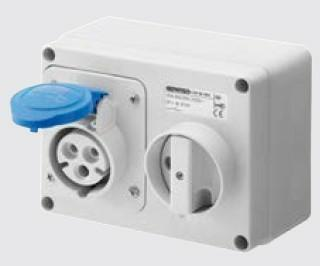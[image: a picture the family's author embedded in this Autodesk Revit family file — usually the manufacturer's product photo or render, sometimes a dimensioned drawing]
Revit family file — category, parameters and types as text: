
# Revit family: Building-IEC309Connections-GEWISS-44IB-INTERLOCKED-SOCKET-OUTLETS_IP44_WITH_BOTTOM
name_source: partatom
category: Apparecchi elettrici
units: mm (PartAtom-declared; Revit-internal decimal feet)

## family parameters
Condiviso = No
Host = Superficie
Mantenere orientamento annotazione = Sì
Punto di calcolo locali = Sì
Quota connettore circolare = Usa diametro
Taglio con vuoti quando caricato = No
Tipo di parte = Normale

## types (22) — shared parameters
BLOCCO = B=C
Catalogue = BUILDING
Catalogue Range = 44 IB
Electrocod = 2220
FORMULA = 1000 mm  [stored 3.28084 ft]
Frequency = 50/60 Hz
Glow Wire Test = 850 °C (active parts) - 650 °C (passive parts)
Glow wire test: = 850 °C (active parts) - 650 °C (passive parts)
IDF = e013b842-d6f1-4fba-800c-bd3a9423ad0b
IDT = 54ab296f-77ff-4020-be1a-67a03cbf098f
IP degree = IP44
Immagine tipo = IP44Fondo.jpg
L = 155 mm  [stored 0.50853 ft]
N_poli = 1
Operating temperature: = -25 +40 °C
POMELLO = bianco
PRESA = Giallo
Produttore = GEWISS S.p.A.
Prospetto di default = 1219 mm
Protection = NO (SBF)
Rated frequency (Hz) = 50/60 Hz
SEO = Socket outlet
STRUTTURA = RAL - 7035
STRUTTURA ALTA = blue
Shock resistance = IK08
Spostamento_S = 500 mm
Technical sheet = https://www.gewiss.com
Thermo-pressure with ball = 125 °C (active parts) - 80 °C (passive parts)
Typology = Horizontal
URL = https://www.gewiss.com
VETRO = Vetro
Version file RFA = 21.4
Voltaggio = 0 V
W = 115 mm  [stored 0.377297 ft]
With back-mounting box = Yes
Working temperature = -25 ÷ +40 °C

## per-type parameters (varying)
| type | Colour | Colour: | Descrizione | EAN code | Modello | No. of poles | Number of poles | Rated current (A) | Rated current (In) | Rated voltage | Reference h |
| GW66009 - 16A 3P+N+E 400V H.INT.SOCK.O.W.B. 6H SBF | Red | Red | 16A 3P+N+E 400V H.INT.SOCK.O.W.B. 6H SBF | 8011564005839 | GW66009 | 3P+N+E | 3P+N+E | 16 | 16 | 380-415V | 6 |
| GW66018 - 32A 2P+E 400V H.INT.SOCK.O.W.B. 9H SBF | Red | Red | 32A 2P+E 400V H.INT.SOCK.O.W.B. 9H SBF | 8011564006157 | GW66018 | 2P+E | 2P+E | 32 | 32 | 380-415V | 9 |
| GW66010 - 16A 3P+E 500V H.INT.SOCK.O.W.B. 7H SBF | Black | Black | 16A 3P+E 500V H.INT.SOCK.O.W.B. 7H SBF | 8011564005860 | GW66010 | 3P+E | 3P+E | 16 | 16 | 480-500V | 7 |
| GW66003 - 16A 3P+N+E 110V H.INT.SOCK.O.W.B. 4H SBF | Yellow | Yellow | 16A 3P+N+E 110V H.INT.SOCK.O.W.B. 4H SBF | 8011564005877 | GW66003 | 3P+N+E | 3P+N+E | 16 | 16 | 100-130V | 4 |
| GW66002 - 16A 3P+E 110V H.INT.SOCK.O.W.B. 4H SBF | Yellow | Yellow | 16A 3P+E 110V H.INT.SOCK.O.W.B. 4H SBF | 8011564005853 | GW66002 | 3P+E | 3P+E | 16 | 16 | 100-130V | 4 |
| GW66005 - 16A 3P+E 230V H.INT.SOCK.O.W.B. 9H SBF | Blue | Blue | 16A 3P+E 230V H.INT.SOCK.O.W.B. 9H SBF | 8011564005815 | GW66005 | 3P+E | 3P+E | 16 | 16 | 200-250V | 9 |
| GW66007 - 16A 2P+E 400V H.INT.SOCK.O.W.B. 9H SBF | Red | Red | 16A 2P+E 400V H.INT.SOCK.O.W.B. 9H SBF | 8011564005846 | GW66007 | 2P+E | 2P+E | 16 | 16 | 380-415V | 9 |
| GW66004 - 16A 2P+E 230V H.INT.SOCK.O.W.B. 6H SBF | Blue | Blue | 16A 2P+E 230V H.INT.SOCK.O.W.B. 6H SBF | 8011564005808 | GW66004 | 2P+E | 2P+E | 16 | 16 | 200-250V | 6 |
| GW66019 - 32A 3P+E 400V H.INT.SOCK.O.W.B. 6H SBF | Red | Red | 32A 3P+E 400V H.INT.SOCK.O.W.B. 6H SBF | 8011564006126 | GW66019 | 3P+E | 3P+E | 32 | 32 | 380-415V | 6 |
| GW66020 - 32A 3P+N+E 400V H.INT.SOCK.O.W.B. 6H SBF | Red | Red | 32A 3P+N+E 400V H.INT.SOCK.O.W.B. 6H SBF | 8011564006133 | GW66020 | 3P+N+E | 3P+N+E | 32 | 32 | 380-415V | 6 |
| GW66001 - 16A 2P+E 110V H.INT.SOCK.O.W.B. 4H SBF | Yellow | Yellow | 16A 2P+E 110V H.INT.SOCK.O.W.B. 4H SBF | 8011564005792 | GW66001 | 2P+E | 2P+E | 16 | 16 | 100-130V | 4 |
| GW66006 - 16A 3P+N+E 230V H.INT.SOCK.O.W.B. 9H SBF | Blue | Blue | 16A 3P+N+E 230V H.INT.SOCK.O.W.B. 9H SBF | 8011564005884 | GW66006 | 3P+N+E | 3P+N+E | 16 | 16 | 200-250V | 9 |
| GW66011 - 16A 3P+N+E 500V H.INT.SOCK.O.W.B. 7H SBF | Black | Black | 16A 3P+N+E 500V H.INT.SOCK.O.W.B. 7H SBF | 8011564006096 | GW66011 | 3P+N+E | 3P+N+E | 16 | 16 | 480-500V | 7 |
| GW66008 - 16A 3P+E 400V H.INT.SOCK.O.W.B. 6H SBF | Red | Red | 16A 3P+E 400V H.INT.SOCK.O.W.B. 6H SBF | 8011564005822 | GW66008 | 3P+E | 3P+E | 16 | 16 | 380-415V | 6 |
| GW66012 - 32A 2P+E 110V H.INT.SOCK.O.W.B. 4H SBF | Yellow | Yellow | 32A 2P+E 110V H.INT.SOCK.O.W.B. 4H SBF | 8011564006140 | GW66012 | 2P+E | 2P+E | 32 | 32 | 100-130V | 4 |
| GW66013 - 32A 3P+E 110V H.INT.SOCK.O.W.B. 4H SBF | Yellow | Yellow | 32A 3P+E 110V H.INT.SOCK.O.W.B. 4H SBF | 8011564006164 | GW66013 | 3P+E | 3P+E | 32 | 32 | 100-130V | 4 |
| GW66014 - 32A 3P+N+E 110V H.INT.SOCK.O.W.B. 4H SBF | Yellow | Yellow | 32A 3P+N+E 110V H.INT.SOCK.O.W.B. 4H SBF | 8011564006195 | GW66014 | 3P+N+E | 3P+N+E | 32 | 32 | 100-130V | 4 |
| GW66021 - 32A 3P+E 500V H.INT.SOCK.O.W.B. 7H SBF | Black | Black | 32A 3P+E 500V H.INT.SOCK.O.W.B. 7H SBF | 8011564006188 | GW66021 | 3P+E | 3P+E | 32 | 32 | 480-500V | 7 |
| GW66017 - 32A 3P+N+E 230V H.INT.SOCK.O.W.B. 9H SBF | Blue | Blue | 32A 3P+N+E 230V H.INT.SOCK.O.W.B. 9H SBF | 8011564006201 | GW66017 | 3P+N+E | 3P+N+E | 32 | 32 | 200-250V | 9 |
| GW66022 - 32A 3P+N+E 500V H.INT.SOCK.O.W.B. 7H SBF | Black | Black | 32A 3P+N+E 500V H.INT.SOCK.O.W.B. 7H SBF | 8011564006218 | GW66022 | 3P+N+E | 3P+N+E | 32 | 32 | 480-500V | 7 |
| GW66016 - 32A 3P+E 230V H.INT.SOCK.O.W.B. 9H SBF | Blue | Blue | 32A 3P+E 230V H.INT.SOCK.O.W.B. 9H SBF | 8011564006171 | GW66016 | 3P+E | 3P+E | 32 | 32 | 200-250V | 9 |
| GW66015 - 32A 2P+E 230V H.INT.SOCK.O.W.B. 6H SBF | Blue | Blue | 32A 2P+E 230V H.INT.SOCK.O.W.B. 6H SBF | 8011564006102 | GW66015 | 2P+E | 2P+E | 32 | 32 | 200-250V | 6 |

note: [stored X ft] marks values corroborated as IEEE doubles in the binary element streams (Revit-internal decimal feet)

## geometry (parser evidence)
native form markers: Sweep x4
no freeform markers — native parametric forms only
